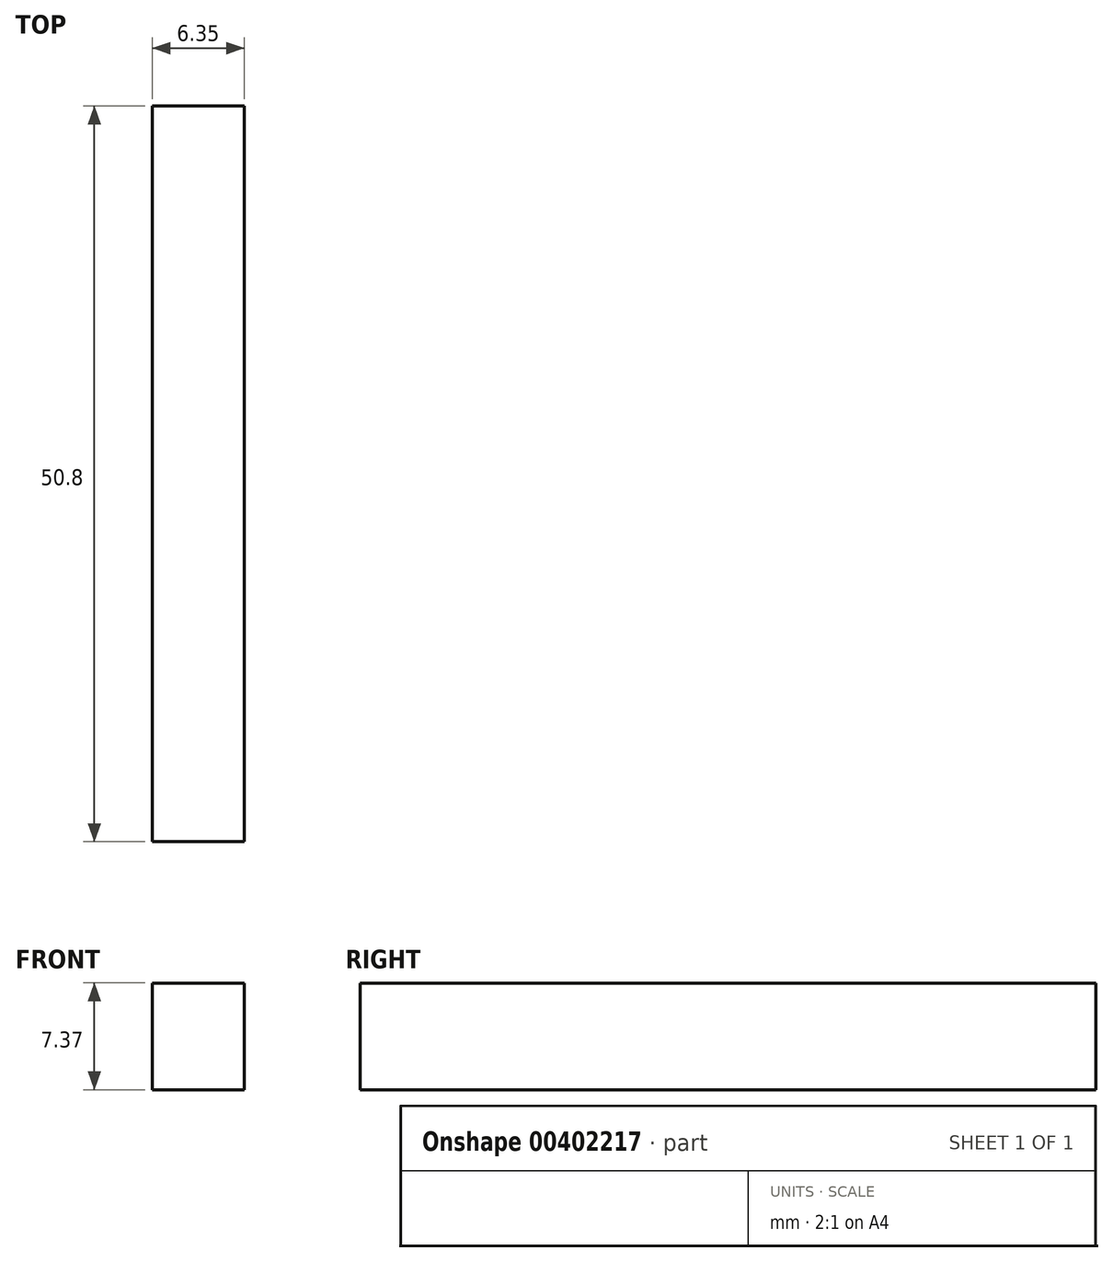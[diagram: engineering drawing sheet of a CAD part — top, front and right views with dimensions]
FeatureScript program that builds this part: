
annotation { "Feature Type Name" : "Feature", "Feature Type Description" : "" }
export const myFeature = defineFeature(function(context is Context, id is Id, definition is map)
    precondition{}
    {
        {
            var Q0;
            Q0=qCreatedBy(makeId("Top.planeOp"),FACE);
            var sketch = newSketch(context, id + "F0", { "sketchPlane" : qUnion([Q0])});
            skLineSegment(sketch, "E0.bottom", {"start": v(0, 0) * mm, "end": v(6.35, 0) * mm});
            skLineSegment(sketch, "E0.top", {"start": v(0, 50.8) * mm, "end": v(6.35, 50.8) * mm});
            skLineSegment(sketch, "E0.left", {"start": v(0, 0) * mm, "end": v(0, 50.8) * mm});
            skLineSegment(sketch, "E0.right", {"start": v(6.35, 0) * mm, "end": v(6.35, 50.8) * mm});
            skSolve(sketch);
        }
        {
            var Q0;
            Q0 = qSketchRegion(id + "F0", true);
            extrude(context, id + "F1", {"entities" : qUnion([Q0]), "depth" : 7.37 * mm});
        }
    });
